# Revit family: NBS_ConceptCubicleSystems_PnlCbclSym_OlympusFullyFramed
name_source: partatom
category: Specialty Equipment
units: mm (PartAtom-declared; Revit-internal decimal feet)

## family parameters
Always vertical = Yes
Cut with Voids When Loaded = No
Part Type = Normal
Room Calculation Point = No
Round Connector Dimension = Use Diameter
Shared = No
Work Plane-Based = No

## types (8) — shared parameters
Application = Designed for use in demanding wet changing environments
AssetType = Fixed
Category = Ss_25_12_60_60:Panel cubicle systems
Description = Fully framed olympus cubicles
DoorLeafMaterial = NBS_ConceptCubicleSystems_B116_BeigeNature-Beige
DurationUnit = year
Features = Black core with a radiused edge, fully framed ironmongery with security fixings, pivoting foot to accomidate for falls in floors, anti-trap hinges
Finish = Powder coated
Fittings = Powder coated aluminium fully framed
FrameMaterial = NBS_ConceptCubicleSystems_PowderCoatedAluminium
IfcExportAs = IfcFurnitureType
IfcExportType = USERDEFINED
IsBuiltIn = Yes
ManufacturerName = Concept Cubicle Systems
ManufacturerURL = www.conceptcubiclesystems.co.uk
Material = Compact Grade Laminate
ModelReference = Olympus Fully Framed Cubicles
NBSCertification = www.nationalbimlibrary.com/cert/4hurcstt
NBSDescription = Panel cubicle system
NBSReference = 25-05-60/160
PanelSupports = 150 mm
PanelThickness = 13 mm
Panels = 12 mm compact grade laminate
PartitionMaterial = NBS_ConceptCubicleSystems_B116_BeigeNature-Beige
PilasterMaterial = NBS_ConceptCubicleSystems_B116_BeigeNature-Beige
ProductInformation = https://www.conceptcubiclesystems.co.uk
Size = 1500 x 2000 mm
Status = UNSET
Style = Cubicle
SystemManufacturer = Concept Cubicle Systems
Uniclass2015Code = Ss_25_12_60_60
Uniclass2015Title = Panel cubicle systems
Uniclass2015Version = Systems v1.17
Version = 3
WarrantyDurationUnit = year

## per-type parameters (varying)
| type | BIMObjectName | HasCornerLeft | HasCornerRight | HasFittingsLeft | HasFittingsRight | HasPartitionLeft | HasPartitionRight | IsEndCubicle | IsFirstCubicle | IsMiddleCubicle | IsSingleCubicle | IsWallEndEndCubicle | IsWallEndFirstCubicle | IsWallEndSingleCubicle | IsWallToWallSingleCubicle | Name | PartitionToPilasterFittingRight | PartitionToPilasterLeft | PartitionToPilasterRight | PilasterPanelReturnLeft | PilasterPanelReturnRight | RailOffsetLeft | RailOffsetRight |
| SingleCubicle | NBS_ConceptCubicleSystems_PanelCubicleSystem_OlympusFullyFramed_SingleCubicle | Yes | Yes | No | No | Yes | Yes | No | No | No | Yes | No | No | No | No | PanelCubicleSystem_OlympusFullyFramed_SingleCubicle_ConceptCubicleSystems | No | 15 mm  [stored 0.0492126 ft] | 15 mm  [stored 0.0492126 ft] | 15 mm  [stored 0.0492126 ft] | 15 mm  [stored 0.0492126 ft] | 25 mm  [stored 0.082021 ft] | 25 mm  [stored 0.082021 ft] |
| WallToWallSingleCubicle | NBS_ConceptCubicleSystems_PanelCubicleSystem_OlympusFullyFramed_WallToWallSingleCubicle | No | No | Yes | Yes | No | No | No | No | No | No | No | No | No | Yes | PanelCubicleSystem_OlympusFullyFramed_WallToWallSingleCubicle_ConceptCubicleSystems | No | 9 mm  [stored 0.0295276 ft] | 9 mm  [stored 0.0295276 ft] | 3 mm  [stored 0.00984252 ft] | 3 mm  [stored 0.00984252 ft] | 0 mm  [stored 0 ft] | 0 mm  [stored 0 ft] |
| EndCubicle | NBS_ConceptCubicleSystems_PanelCubicleSystem_OlympusFullyFramed_EndCubicle | No | Yes | No | No | No | Yes | Yes | No | No | No | No | No | No | No | PanelCubicleSystem_OlympusFullyFramed_EndCubicle_ConceptCubicleSystems | No | 9 mm  [stored 0.0295276 ft] | 15 mm  [stored 0.0492126 ft] | 0 mm  [stored 0 ft] | 15 mm  [stored 0.0492126 ft] | 0 mm  [stored 0 ft] | 25 mm  [stored 0.082021 ft] |
| FirstCubicle | NBS_ConceptCubicleSystems_PanelCubicleSystem_OlympusFullyFramed_FirstCubicle | Yes | No | No | No | Yes | Yes | No | Yes | No | No | No | No | No | No | PanelCubicleSystem_OlympusFullyFramed_FirstCubicle_ConceptCubicleSystems | Yes | 15 mm  [stored 0.0492126 ft] | 9 mm  [stored 0.0295276 ft] | 15 mm  [stored 0.0492126 ft] | 0 mm  [stored 0 ft] | 25 mm  [stored 0.082021 ft] | 0 mm  [stored 0 ft] |
| WallEndFirstCubicle | NBS_ConceptCubicleSystems_PanelCubicleSystem_OlympusFullyFramed_WallEndFirstCubicle | No | No | Yes | No | No | Yes | No | No | No | No | No | Yes | No | No | PanelCubicleSystem_OlympusFullyFramed_WallEndFirstCubicle_ConceptCubicleSystems | Yes | 9 mm  [stored 0.0295276 ft] | 9 mm  [stored 0.0295276 ft] | 3 mm  [stored 0.00984252 ft] | 0 mm  [stored 0 ft] | 0 mm  [stored 0 ft] | 0 mm  [stored 0 ft] |
| WallEndSingleCubicle | NBS_ConceptCubicleSystems_PanelCubicleSystem_OlympusFullyFramed_WallEndSingleCubicle | No | Yes | Yes | No | No | Yes | No | No | No | No | No | No | Yes | No | PanelCubicleSystem_OlympusFullyFramed_WallEndSingleCubicle_ConceptCubicleSystems | No | 9 mm  [stored 0.0295276 ft] | 15 mm  [stored 0.0492126 ft] | 3 mm  [stored 0.00984252 ft] | 15 mm  [stored 0.0492126 ft] | 0 mm  [stored 0 ft] | 25 mm  [stored 0.082021 ft] |
| MiddleCubicle | NBS_ConceptCubicleSystems_PanelCubicleSystem_OlympusFullyFramed_MiddleCubicle | No | No | No | No | No | Yes | No | No | Yes | No | No | No | No | No | PanelCubicleSystem_OlympusFullyFramed_MiddleCubicle_ConceptCubicleSystems | Yes | 9 mm  [stored 0.0295276 ft] | 9 mm  [stored 0.0295276 ft] | 0 mm  [stored 0 ft] | 0 mm  [stored 0 ft] | 0 mm  [stored 0 ft] | 0 mm  [stored 0 ft] |
| WallEndEndCubicle | NBS_ConceptCubicleSystems_PanelCubicleSystem_OlympusFullyFramed_WallEndEndCubicle | No | No | No | Yes | No | No | No | No | No | No | Yes | No | No | No | PanelCubicleSystem_OlympusFullyFramed_WallEndEndCubicle_ConceptCubicleSystems | No | 9 mm  [stored 0.0295276 ft] | 9 mm  [stored 0.0295276 ft] | 0 mm  [stored 0 ft] | 3 mm  [stored 0.00984252 ft] | 0 mm  [stored 0 ft] | 0 mm  [stored 0 ft] |

note: [stored X ft] marks values corroborated as IEEE doubles in the binary element streams (Revit-internal decimal feet)

## geometry (parser evidence)
native form markers: Sweep x4
no freeform markers — native parametric forms only
